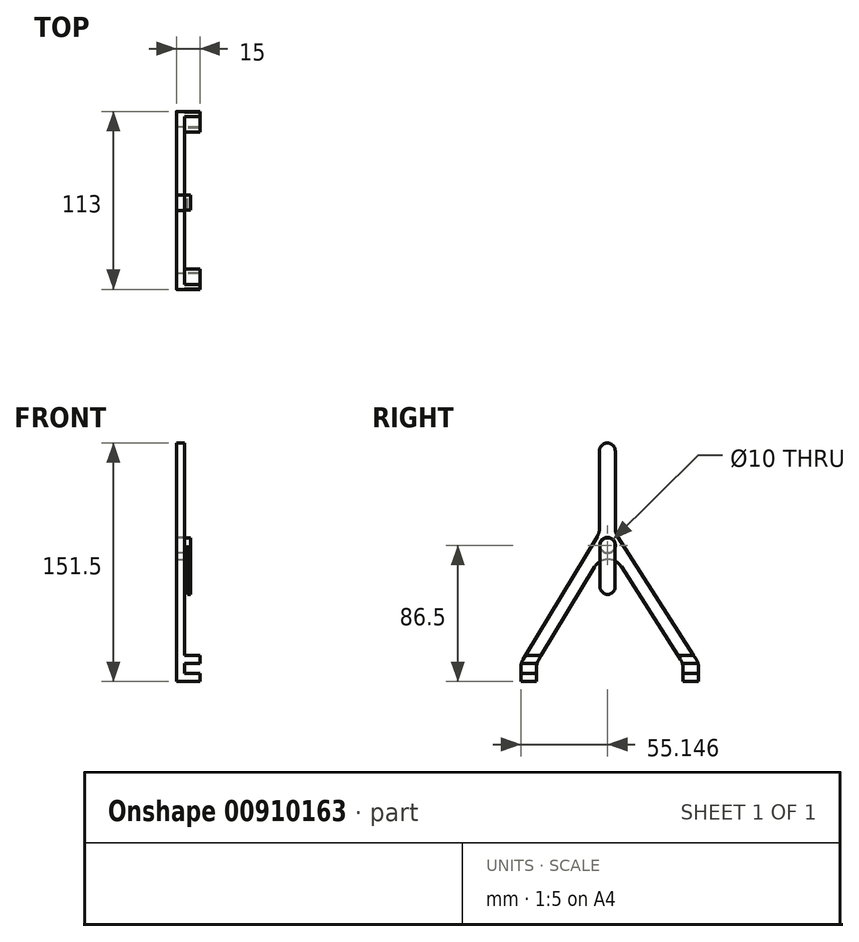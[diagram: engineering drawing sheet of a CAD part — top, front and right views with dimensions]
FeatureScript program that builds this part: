
annotation { "Feature Type Name" : "Feature", "Feature Type Description" : "" }
export const myFeature = defineFeature(function(context is Context, id is Id, definition is map)
    precondition{}
    {
        {
            var Q0;
            Q0=qCreatedBy(makeId("Right.planeOp"),FACE);
            cPlane(context, id + "F0", {"entities" : qUnion([Q0]), "cplaneType" : CPlaneType.OFFSET, "offset" : 70 * mm, "oppositeDirection" : true, "width" : 150 * mm, "height" : 150 * mm});
        }
        {
            var Q0;
            Q0=qCreatedBy(id+"F0.planeOp",FACE);
            var sketch = newSketch(context, id + "F1", { "sketchPlane" : qUnion([Q0])});
            skLineSegment(sketch, "E0", {"start": v(0.15, 75) * mm, "end": v(-45, 0) * mm});
            skLineSegment(sketch, "E1", {"start": v(-55, -11.5) * mm, "end": v(-55, 0) * mm});
            skLineSegment(sketch, "E2", {"start": v(-55, 0) * mm, "end": v(-5, 83.06) * mm});
            skLineSegment(sketch, "E3", {"start": v(-5, 83.06) * mm, "end": v(-5, 140) * mm});
            skLineSegment(sketch, "E4", {"start": v(-5, 140) * mm, "end": v(0, 140) * mm});
            skLineSegment(sketch, "E5", {"start": v(0, 140) * mm, "end": v(5, 140) * mm});
            skLineSegment(sketch, "E6", {"start": v(5, 140) * mm, "end": v(5, 83.06) * mm});
            skLineSegment(sketch, "E7", {"start": v(5, 83.06) * mm, "end": v(58, 0) * mm});
            skLineSegment(sketch, "E8", {"start": v(58, -11.5) * mm, "end": v(48, -11.5) * mm});
            skLineSegment(sketch, "E9", {"start": v(48, -11.5) * mm, "end": v(48, 0) * mm});
            skLineSegment(sketch, "E10", {"start": v(48, 0) * mm, "end": v(0.15, 75) * mm});
            skLineSegment(sketch, "E11", {"start": v(-55, -11.5) * mm, "end": v(-45, -11.5) * mm});
            skLineSegment(sketch, "E12", {"start": v(-45, -11.5) * mm, "end": v(-45, 0) * mm});
            skLineSegment(sketch, "E13", {"start": v(58, 0) * mm, "end": v(58, -11.5) * mm});
            skSolve(sketch);
        }
        {
            var Q0;
            Q0=makeQuery(id+"F1.imprint","IMPRINT",FACE,{"disambiguationData":[TD([[makeQuery(id+"F1.imprint","IMPRINT",EDGE,{"derivedFrom":sQuery(id+"F1.wireOp",EDGE,"E0")}),-1.0]])]});
            extrude(context, id + "F2", {"entities" : qUnion([Q0]), "depth" : 5 * mm, "offsetDistance" : 25 * mm});
        }
        {
            var Q0;
            Q0=makeQuery(id+"F2.opExtrude","SWEPT_EDGE",EDGE,{"disambiguationData":[OSD([sQuery(id+"F1.wireOp",EDGE,"E0"),sQuery(id+"F1.wireOp",EDGE,"2Qdq0gd9-1Wts-JzQb-aNDY-cJtiMOODCq13")])]});
            var Q1;
            Q1=makeQuery(id+"F2.opExtrude","SWEPT_EDGE",EDGE,{"disambiguationData":[OSD([sQuery(id+"F1.wireOp",EDGE,"E1"),sQuery(id+"F1.wireOp",EDGE,"E2")])]});
            var Q2;
            Q2=makeQuery(id+"F2.opExtrude","SWEPT_EDGE",EDGE,{"disambiguationData":[OSD([sQuery(id+"F1.wireOp",EDGE,"E9"),sQuery(id+"F1.wireOp",EDGE,"E10")])]});
            var Q3;
            Q3=makeQuery(id+"F2.opExtrude","SWEPT_EDGE",EDGE,{"disambiguationData":[OSD([sQuery(id+"F1.wireOp",EDGE,"E7"),sQuery(id+"F1.wireOp",EDGE,"AGq9xMHe-UfYn-AV5J-j3cz-IK4XJuOyjXgd")])]});
            var Q4;
            Q4=makeQuery(id+"F2.opExtrude","SWEPT_EDGE",EDGE,{"disambiguationData":[OSD([sQuery(id+"F1.wireOp",EDGE,"E0"),sQuery(id+"F1.wireOp",EDGE,"E10")])]});
            var Q5;
            Q5=makeQuery(id+"F2.opExtrude","SWEPT_EDGE",EDGE,{"disambiguationData":[OSD([sQuery(id+"F1.wireOp",EDGE,"E6"),sQuery(id+"F1.wireOp",EDGE,"E7")])]});
            var Q6;
            Q6=makeQuery(id+"F2.opExtrude","SWEPT_EDGE",EDGE,{"disambiguationData":[OSD([sQuery(id+"F1.wireOp",EDGE,"E2"),sQuery(id+"F1.wireOp",EDGE,"E3")])]});
            fillet(context, id + "F3", {"entities" : qUnion([Q0, Q1, Q2, Q3, Q4, Q5, Q6]), "radius" : 10 * mm, "tangentPropagation" : true, "allowEdgeOverflow" : false});
        }
        {
            var Q0;
            Q0=makeQuery(id+"F2.opExtrude","SWEPT_EDGE",EDGE,{"disambiguationData":[OSD([sQuery(id+"F1.wireOp",EDGE,"E3"),sQuery(id+"F1.wireOp",EDGE,"E4")])]});
            var Q1;
            Q1=makeQuery(id+"F2.opExtrude","SWEPT_EDGE",EDGE,{"disambiguationData":[OSD([sQuery(id+"F1.wireOp",EDGE,"E5"),sQuery(id+"F1.wireOp",EDGE,"E6")])]});
            fillet(context, id + "F4", {"entities" : qUnion([Q0, Q1]), "radius" : 5 * mm, "tangentPropagation" : true, "allowEdgeOverflow" : false});
        }
        {
            var Q0;
            Q0=makeQuery(id+"F2.opExtrude","CAP_FACE",FACE,{"disambiguationData":[OSD([sQuery(id+"F1.wireOp",EDGE,"E0"),sQuery(id+"F1.wireOp",EDGE,"2Qdq0gd9-1Wts-JzQb-aNDY-cJtiMOODCq13"),sQuery(id+"F1.wireOp",EDGE,"tQ7Qx2Js-TAmm-NFPa-ttCH-rFNCJ0qlS3tg"),sQuery(id+"F1.wireOp",EDGE,"E1"),sQuery(id+"F1.wireOp",EDGE,"E2"),sQuery(id+"F1.wireOp",EDGE,"E3"),sQuery(id+"F1.wireOp",EDGE,"E4"),sQuery(id+"F1.wireOp",EDGE,"E5"),sQuery(id+"F1.wireOp",EDGE,"E6"),sQuery(id+"F1.wireOp",EDGE,"E7"),sQuery(id+"F1.wireOp",EDGE,"AGq9xMHe-UfYn-AV5J-j3cz-IK4XJuOyjXgd"),sQuery(id+"F1.wireOp",EDGE,"E8"),sQuery(id+"F1.wireOp",EDGE,"E9"),sQuery(id+"F1.wireOp",EDGE,"E10")])],"isStart":false});
            var sketch = newSketch(context, id + "F5", { "sketchPlane" : qUnion([Q0])});
            skLineSegment(sketch, "E14.bottom", {"start": v(-55, -11.5) * mm, "end": v(-45, -11.5) * mm});
            skLineSegment(sketch, "E14.top", {"start": v(-55, -6.5) * mm, "end": v(-45, -6.5) * mm});
            skLineSegment(sketch, "E14.left", {"start": v(-55, -11.5) * mm, "end": v(-55, -6.5) * mm});
            skLineSegment(sketch, "E14.right", {"start": v(-45, -11.5) * mm, "end": v(-45, -6.5) * mm});
            skLineSegment(sketch, "E15", {"start": v(-54.6, 0) * mm, "end": v(-39.56, 0) * mm});
            skLineSegment(sketch, "E16", {"start": v(-52, 5) * mm, "end": v(-42, 5) * mm});
            skLineSegment(sketch, "E17", {"start": v(44.8, 5) * mm, "end": v(54.8, 5) * mm});
            skLineSegment(sketch, "E18", {"start": v(48, -6.5) * mm, "end": v(58, -6.5) * mm});
            skLineSegment(sketch, "E19", {"start": v(58, -6.5) * mm, "end": v(58, -11.5) * mm});
            skLineSegment(sketch, "E20", {"start": v(58, -11.5) * mm, "end": v(48, -11.5) * mm});
            skLineSegment(sketch, "E21", {"start": v(48, -11.5) * mm, "end": v(48, -6.5) * mm});
            skLineSegment(sketch, "E22", {"start": v(47.56, 0) * mm, "end": v(57.56, 0) * mm});
            skSolve(sketch);
        }
        {
            var Q0;
            Q0=qSketchRegion(id+"F5",true);
            var Q1;
            {var subQ8=sQuery(id+"F5.wireOp",EDGE,"E15");Q1=makeQuery(id+"F5.imprint","IMPRINT",FACE,{"disambiguationData":[TD([[makeQuery(id+"F5.imprint","IMPRINT",EDGE,{"derivedFrom":subQ8}),1.0]])]});}
            var Q2;
            {var subQ12=sQuery(id+"F5.wireOp",EDGE,"E17");Q2=makeQuery(id+"F5.imprint","IMPRINT",FACE,{"disambiguationData":[TD([[makeQuery(id+"F5.imprint","IMPRINT",EDGE,{"derivedFrom":subQ12}),-1.0]])]});}
            extrude(context, id + "F6", {"entities" : qUnion([Q0, Q1, Q2]), "operationType" : NewBodyOperationType.ADD, "depth" : 10 * mm, "offsetDistance" : 25 * mm});
        }
        {
            var Q0;
            Q0=makeQuery(id+"F1.imprint","IMPRINT",FACE,{"disambiguationData":[TD([[makeQuery(id+"F1.imprint","IMPRINT",EDGE,{"derivedFrom":sQuery(id+"F1.wireOp",EDGE,"E0")}),-1.0]])]});
            var sketch = newSketch(context, id + "F7", { "sketchPlane" : qUnion([Q0])});
            skCircle(sketch, "E23", {"center": v(0.15, 75) * mm, "radius": 5 * mm});
            skSolve(sketch);
        }
        {
            var Q0;
            {var subQ0=sQuery(id+"F7.wireOp",EDGE,"E23");var subQ1=makeQuery(id+"F1.imprint","IMPRINT",EDGE,{"derivedFrom":sQuery(id+"F1.wireOp",EDGE,"E0")});var subQ2=makeQuery(id+"F7.imprint","INTERSECT",VERTEX,{"derivedFrom":[subQ1,subQ0]});Q0=makeQuery(id+"F7.imprint","IMPRINT",FACE,{"disambiguationData":[TD([[makeQuery(id+"F7.imprint","IMPRINT",EDGE,{"disambiguationData":[TD([[subQ2,1.0]])],"derivedFrom":subQ0}),1.0]])]});}
            var Q1;
            {var subQ0=sQuery(id+"F7.wireOp",EDGE,"E23");var subQ1=makeQuery(id+"F1.imprint","IMPRINT",EDGE,{"derivedFrom":sQuery(id+"F1.wireOp",EDGE,"E0")});var subQ2=makeQuery(id+"F7.imprint","INTERSECT",VERTEX,{"derivedFrom":[subQ1,subQ0]});Q1=makeQuery(id+"F7.imprint","IMPRINT",FACE,{"disambiguationData":[TD([[makeQuery(id+"F7.imprint","IMPRINT",EDGE,{"disambiguationData":[TD([[subQ2,-1.0]])],"derivedFrom":subQ0}),1.0]])]});}
            var Q2;
            Q2=sQuery(id+"F7.wireOp",EDGE,"E23");
            extrude(context, id + "F8", {"entities" : qUnion([Q0, Q1]), "operationType" : NewBodyOperationType.REMOVE, "surfaceEntities" : qUnion([Q2]), "endBound" : BoundingType.UP_TO_NEXT, "depth" : 25 * mm, "offsetDistance" : 25 * mm});
        }
        {
            var Q0;
            {var subQ0=sQuery(id+"F7.wireOp",EDGE,"E23");var subQ1=makeQuery(id+"F1.imprint","IMPRINT",EDGE,{"derivedFrom":sQuery(id+"F1.wireOp",EDGE,"E0")});var subQ2=makeQuery(id+"F7.imprint","INTERSECT",VERTEX,{"derivedFrom":[subQ1,subQ0]});Q0=makeQuery(id+"F7.imprint","IMPRINT",FACE,{"disambiguationData":[TD([[makeQuery(id+"F7.imprint","IMPRINT",EDGE,{"disambiguationData":[TD([[subQ2,1.0]])],"derivedFrom":subQ0}),1.0]])]});}
            var sketch = newSketch(context, id + "F9", { "sketchPlane" : qUnion([Q0])});
            skCircle(sketch, "E24", {"center": v(0.15, 75) * mm, "radius": 4.8 * mm});
            skSolve(sketch);
        }
        {
            var Q0;
            Q0 = qSketchRegion(id + "F9", true);
            extrude(context, id + "F10", {"entities" : qUnion([Q0]), "depth" : 9 * mm, "offsetDistance" : 25 * mm});
        }
        {
            var Q0;
            Q0=makeQuery(id+"F10.opExtrude","CAP_FACE",FACE,{"disambiguationData":[OSD([sQuery(id+"F9.wireOp",EDGE,"E24")])],"isStart":false});
            var sketch = newSketch(context, id + "F11", { "sketchPlane" : qUnion([Q0])});
            skLineSegment(sketch, "E25.bottom", {"start": v(-4.65, 75) * mm, "end": v(4.95, 75) * mm});
            skLineSegment(sketch, "E25.top", {"start": v(-4.65, 48.6) * mm, "end": v(4.95, 48.6) * mm});
            skLineSegment(sketch, "E25.left", {"start": v(-4.65, 75) * mm, "end": v(-4.65, 48.6) * mm});
            skLineSegment(sketch, "E25.right", {"start": v(4.95, 75) * mm, "end": v(4.95, 48.6) * mm});
            skCircle(sketch, "E26", {"center": v(0.15, 48.6) * mm, "radius": 4.8 * mm});
            skSolve(sketch);
        }
        {
            var Q0;
            Q0 = qSketchRegion(id + "F11", true);
            var Q1;
            {var subQ0=sQuery(id+"F11.wireOp",EDGE,"E25.bottom");Q1=makeQuery(id+"F11.imprint","IMPRINT",FACE,{"disambiguationData":[TD([[makeQuery(id+"F11.imprint","IMPRINT",EDGE,{"derivedFrom":subQ0}),1.0]])]});}
            extrude(context, id + "F12", {"entities" : qUnion([Q0, Q1]), "operationType" : NewBodyOperationType.ADD, "oppositeDirection" : true, "depth" : 2 * mm, "offsetDistance" : 25 * mm});
        }
    });
